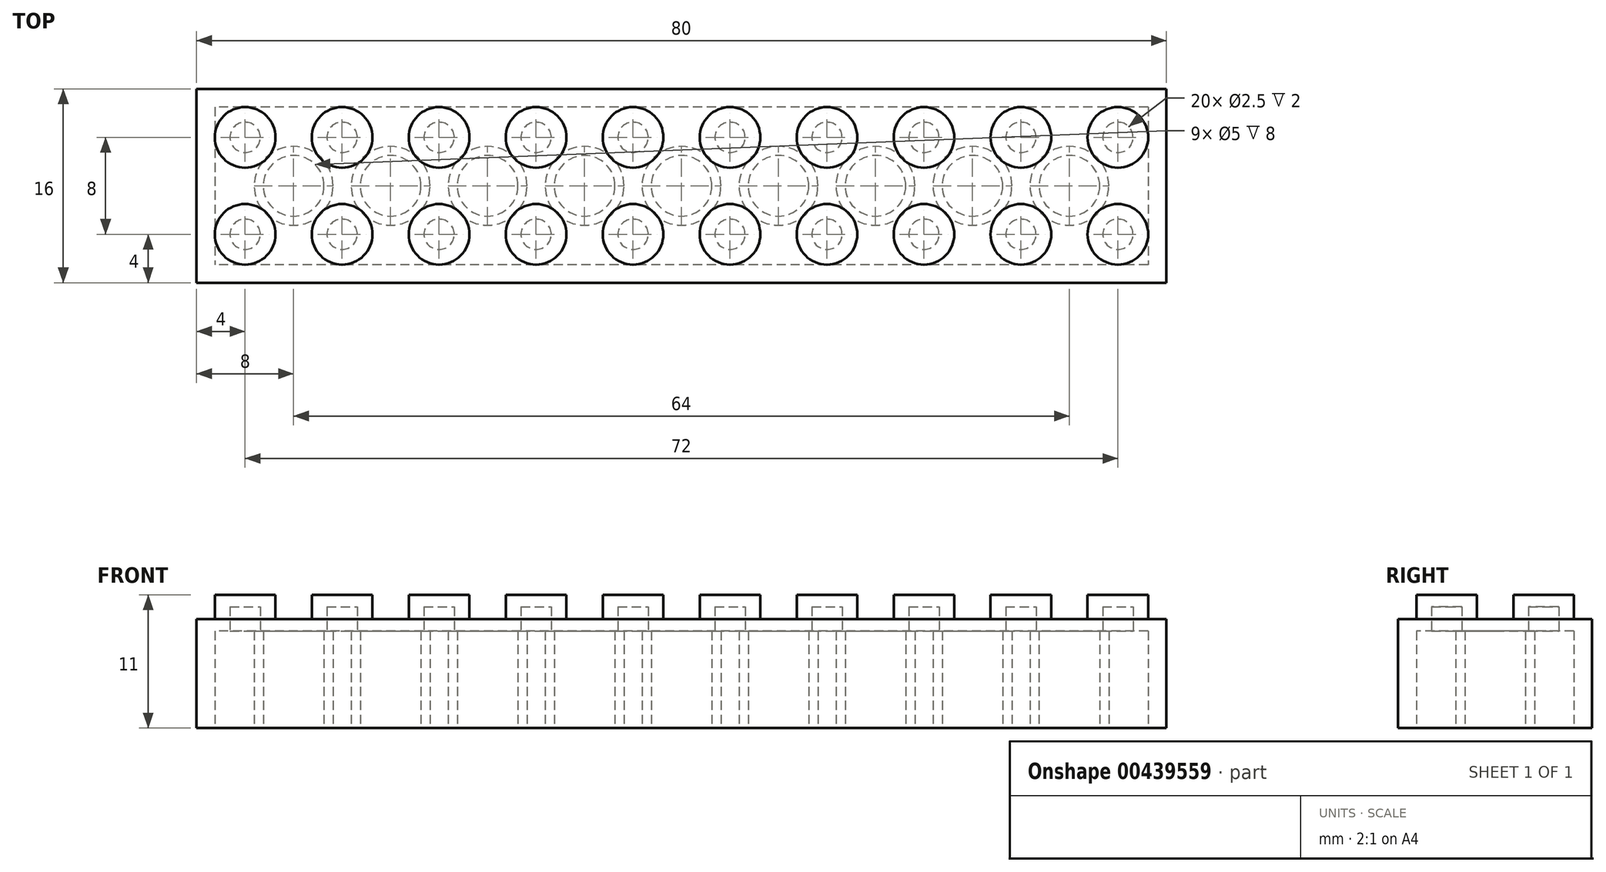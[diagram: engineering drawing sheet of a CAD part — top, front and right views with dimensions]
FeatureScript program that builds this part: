
annotation { "Feature Type Name" : "Feature", "Feature Type Description" : "" }
export const myFeature = defineFeature(function(context is Context, id is Id, definition is map)
    precondition{}
    {
        {
            var Q0;
            Q0=qCreatedBy(makeId("Top.planeOp"),FACE);
            var sketch = newSketch(context, id + "F0", { "sketchPlane" : qUnion([Q0])});
            skLineSegment(sketch, "E0.bottom", {"start": v(40, -8) * mm, "end": v(-40, -8) * mm});
            skLineSegment(sketch, "E0.top", {"start": v(40, 8) * mm, "end": v(-40, 8) * mm});
            skLineSegment(sketch, "E0.left", {"start": v(40, -8) * mm, "end": v(40, 8) * mm});
            skLineSegment(sketch, "E0.right", {"start": v(-40, -8) * mm, "end": v(-40, 8) * mm});
            skPoint(sketch, "E0.middle", {"position": v(0, 0) * mm});
            skSolve(sketch);
        }
        {
            var Q0;
            Q0=makeQuery(id+"F0.imprint","IMPRINT",FACE,{"disambiguationData":[TD([[makeQuery(id+"F0.imprint","IMPRINT",EDGE,{"derivedFrom":sQuery(id+"F0.wireOp",EDGE,"E0.bottom")}),-1.0]])]});
            extrude(context, id + "F1", {"entities" : qUnion([Q0]), "depth" : 9 * mm});
        }
        {
            var Q0;
            Q0=makeQuery(id+"F1.opExtrude","CAP_FACE",FACE,{"disambiguationData":[OSD([sQuery(id+"F0.wireOp",EDGE,"E0.bottom"),sQuery(id+"F0.wireOp",EDGE,"E0.top"),sQuery(id+"F0.wireOp",EDGE,"E0.left"),sQuery(id+"F0.wireOp",EDGE,"E0.right")])],"isStart":false});
            var sketch = newSketch(context, id + "F2", { "sketchPlane" : qUnion([Q0])});
            skCircle(sketch, "E1", {"center": v(-36, 4) * mm, "radius": 2.5 * mm});
            skCircle(sketch, "E2.0.1.0", {"center": v(-36, -4) * mm, "radius": 2.5 * mm});
            skCircle(sketch, "E2.1.0.0", {"center": v(-28, 4) * mm, "radius": 2.5 * mm});
            skCircle(sketch, "E2.1.1.0", {"center": v(-28, -4) * mm, "radius": 2.5 * mm});
            skCircle(sketch, "E2.2.0.0", {"center": v(-20, 4) * mm, "radius": 2.5 * mm});
            skCircle(sketch, "E2.2.1.0", {"center": v(-20, -4) * mm, "radius": 2.5 * mm});
            skCircle(sketch, "E2.3.0.0", {"center": v(-12, 4) * mm, "radius": 2.5 * mm});
            skCircle(sketch, "E2.3.1.0", {"center": v(-12, -4) * mm, "radius": 2.5 * mm});
            skCircle(sketch, "E2.4.0.0", {"center": v(-4, 4) * mm, "radius": 2.5 * mm});
            skCircle(sketch, "E2.4.1.0", {"center": v(-4, -4) * mm, "radius": 2.5 * mm});
            skCircle(sketch, "E2.5.0.0", {"center": v(4, 4) * mm, "radius": 2.5 * mm});
            skCircle(sketch, "E2.5.1.0", {"center": v(4, -4) * mm, "radius": 2.5 * mm});
            skCircle(sketch, "E2.6.0.0", {"center": v(12, 4) * mm, "radius": 2.5 * mm});
            skCircle(sketch, "E2.6.1.0", {"center": v(12, -4) * mm, "radius": 2.5 * mm});
            skCircle(sketch, "E2.7.0.0", {"center": v(20, 4) * mm, "radius": 2.5 * mm});
            skCircle(sketch, "E2.7.1.0", {"center": v(20, -4) * mm, "radius": 2.5 * mm});
            skLineSegment(sketch, "E2.direction1", {"start": v(-36, 4) * mm, "end": v(-28, 4) * mm, "construction": true});
            skLineSegment(sketch, "E2.direction2", {"start": v(-36, 4) * mm, "end": v(-36, -4) * mm, "construction": true});
            skCircle(sketch, "E3.0.8.0", {"center": v(28, 4) * mm, "radius": 2.5 * mm});
            skCircle(sketch, "E3.0.8.1", {"center": v(28, -4) * mm, "radius": 2.5 * mm});
            skCircle(sketch, "E3.0.9.0", {"center": v(36, 4) * mm, "radius": 2.5 * mm});
            skCircle(sketch, "E3.0.9.1", {"center": v(36, -4) * mm, "radius": 2.5 * mm});
            skSolve(sketch);
        }
        {
            var Q0;
            Q0 = qSketchRegion(id + "F2", true);
            extrude(context, id + "F3", {"entities" : qUnion([Q0]), "operationType" : NewBodyOperationType.ADD, "depth" : 2 * mm});
        }
        {
            var Q0;
            Q0=makeQuery(id+"F1.opExtrude","CAP_FACE",FACE,{"disambiguationData":[OSD([sQuery(id+"F0.wireOp",EDGE,"E0.bottom"),sQuery(id+"F0.wireOp",EDGE,"E0.top"),sQuery(id+"F0.wireOp",EDGE,"E0.left"),sQuery(id+"F0.wireOp",EDGE,"E0.right")])],"isStart":true});
            var sketch = newSketch(context, id + "F4", { "sketchPlane" : qUnion([Q0])});
            skLineSegment(sketch, "E4.bottom", {"start": v(38.5, -6.5) * mm, "end": v(-38.5, -6.5) * mm});
            skLineSegment(sketch, "E4.top", {"start": v(38.5, 6.5) * mm, "end": v(-38.5, 6.5) * mm});
            skLineSegment(sketch, "E4.left", {"start": v(38.5, -6.5) * mm, "end": v(38.5, 6.5) * mm});
            skLineSegment(sketch, "E4.right", {"start": v(-38.5, -6.5) * mm, "end": v(-38.5, 6.5) * mm});
            skPoint(sketch, "E4.middle", {"position": v(0, 0) * mm});
            skCircle(sketch, "E5", {"center": v(-32, 0) * mm, "radius": 3.25 * mm});
            skCircle(sketch, "E6", {"center": v(-32, 0) * mm, "radius": 2.5 * mm});
            skCircle(sketch, "E7.1.0.0", {"center": v(-24, 0) * mm, "radius": 3.25 * mm});
            skCircle(sketch, "E7.1.0.1", {"center": v(-24, 0) * mm, "radius": 2.5 * mm});
            skCircle(sketch, "E7.2.0.0", {"center": v(-16, 0) * mm, "radius": 3.25 * mm});
            skCircle(sketch, "E7.2.0.1", {"center": v(-16, 0) * mm, "radius": 2.5 * mm});
            skCircle(sketch, "E7.3.0.0", {"center": v(-8, 0) * mm, "radius": 3.25 * mm});
            skCircle(sketch, "E7.3.0.1", {"center": v(-8, 0) * mm, "radius": 2.5 * mm});
            skCircle(sketch, "E7.4.0.0", {"center": v(0, 0) * mm, "radius": 3.25 * mm});
            skCircle(sketch, "E7.4.0.1", {"center": v(0, 0) * mm, "radius": 2.5 * mm});
            skCircle(sketch, "E7.5.0.0", {"center": v(8, 0) * mm, "radius": 3.25 * mm});
            skCircle(sketch, "E7.5.0.1", {"center": v(8, 0) * mm, "radius": 2.5 * mm});
            skCircle(sketch, "E7.6.0.0", {"center": v(16, 0) * mm, "radius": 3.25 * mm});
            skCircle(sketch, "E7.6.0.1", {"center": v(16, 0) * mm, "radius": 2.5 * mm});
            skLineSegment(sketch, "E7.direction1", {"start": v(-32, 0) * mm, "end": v(-24, 0) * mm, "construction": true});
            skCircle(sketch, "E8.0.7.0", {"center": v(24, 0) * mm, "radius": 3.25 * mm});
            skCircle(sketch, "E8.2.7.0", {"center": v(24, 0) * mm, "radius": 2.5 * mm});
            skCircle(sketch, "E8.0.8.0", {"center": v(32, 0) * mm, "radius": 3.25 * mm});
            skCircle(sketch, "E8.2.8.0", {"center": v(32, 0) * mm, "radius": 2.5 * mm});
            skSolve(sketch);
        }
        {
            var Q0;
            Q0=qSketchRegion(id+"F4",true);
            var Q1;
            Q1=makeQuery(id+"F4.imprint","IMPRINT",FACE,{"disambiguationData":[TD([[makeQuery(id+"F4.imprint","IMPRINT",EDGE,{"derivedFrom":sQuery(id+"F4.wireOp",EDGE,"E6")}),1.0]])]});
            var Q2;
            Q2=makeQuery(id+"F4.imprint","IMPRINT",FACE,{"disambiguationData":[TD([[makeQuery(id+"F4.imprint","IMPRINT",EDGE,{"derivedFrom":sQuery(id+"F4.wireOp",EDGE,"E7.1.0.1")}),1.0]])]});
            var Q3;
            Q3=makeQuery(id+"F4.imprint","IMPRINT",FACE,{"disambiguationData":[TD([[makeQuery(id+"F4.imprint","IMPRINT",EDGE,{"derivedFrom":sQuery(id+"F4.wireOp",EDGE,"E7.2.0.1")}),1.0]])]});
            var Q4;
            Q4=makeQuery(id+"F4.imprint","IMPRINT",FACE,{"disambiguationData":[TD([[makeQuery(id+"F4.imprint","IMPRINT",EDGE,{"derivedFrom":sQuery(id+"F4.wireOp",EDGE,"E7.3.0.1")}),1.0]])]});
            var Q5;
            Q5=makeQuery(id+"F4.imprint","IMPRINT",FACE,{"disambiguationData":[TD([[makeQuery(id+"F4.imprint","IMPRINT",EDGE,{"derivedFrom":sQuery(id+"F4.wireOp",EDGE,"E7.4.0.1")}),1.0]])]});
            var Q6;
            Q6=makeQuery(id+"F4.imprint","IMPRINT",FACE,{"disambiguationData":[TD([[makeQuery(id+"F4.imprint","IMPRINT",EDGE,{"derivedFrom":sQuery(id+"F4.wireOp",EDGE,"E7.5.0.1")}),1.0]])]});
            var Q7;
            Q7=makeQuery(id+"F4.imprint","IMPRINT",FACE,{"disambiguationData":[TD([[makeQuery(id+"F4.imprint","IMPRINT",EDGE,{"derivedFrom":sQuery(id+"F4.wireOp",EDGE,"E7.6.0.1")}),1.0]])]});
            var Q8;
            Q8=makeQuery(id+"F4.imprint","IMPRINT",FACE,{"disambiguationData":[TD([[makeQuery(id+"F4.imprint","IMPRINT",EDGE,{"derivedFrom":sQuery(id+"F4.wireOp",EDGE,"E8.2.7.0")}),1.0]])]});
            var Q9;
            Q9=makeQuery(id+"F4.imprint","IMPRINT",FACE,{"disambiguationData":[TD([[makeQuery(id+"F4.imprint","IMPRINT",EDGE,{"derivedFrom":sQuery(id+"F4.wireOp",EDGE,"E8.2.8.0")}),1.0]])]});
            extrude(context, id + "F5", {"entities" : qUnion([Q0, Q1, Q2, Q3, Q4, Q5, Q6, Q7, Q8, Q9]), "operationType" : NewBodyOperationType.REMOVE, "oppositeDirection" : true, "depth" : 8 * mm});
        }
        {
            var Q0;
            {var subQ0=sQuery(id+"F0.wireOp",EDGE,"E0.left");var subQ1=sQuery(id+"F0.wireOp",EDGE,"E0.top");var subQ2=sQuery(id+"F0.wireOp",EDGE,"E0.right");var subQ3=sQuery(id+"F0.wireOp",EDGE,"E0.bottom");Q0=makeQuery(id+"F5.boolean.opBoolean","SPLIT",FACE,{"disambiguationData":[TD([makeQuery(id+"F1.opExtrude","SWEPT_FACE",FACE,{"disambiguationData":[OSD([subQ3])]})])],"derivedFrom":makeQuery(id+"F1.opExtrude","CAP_FACE",FACE,{"disambiguationData":[OSD([subQ3,subQ1,subQ0,subQ2])],"isStart":true})});}
            var sketch = newSketch(context, id + "F6", { "sketchPlane" : qUnion([Q0])});
            skCircle(sketch, "E9", {"center": v(-36, 4) * mm, "radius": 1.25 * mm});
            skCircle(sketch, "E10.0.1.0", {"center": v(-36, -4) * mm, "radius": 1.25 * mm});
            skCircle(sketch, "E10.1.0.0", {"center": v(-28, 4) * mm, "radius": 1.25 * mm});
            skCircle(sketch, "E10.1.1.0", {"center": v(-28, -4) * mm, "radius": 1.25 * mm});
            skCircle(sketch, "E10.2.0.0", {"center": v(-20, 4) * mm, "radius": 1.25 * mm});
            skCircle(sketch, "E10.2.1.0", {"center": v(-20, -4) * mm, "radius": 1.25 * mm});
            skCircle(sketch, "E10.3.0.0", {"center": v(-12, 4) * mm, "radius": 1.25 * mm});
            skCircle(sketch, "E10.3.1.0", {"center": v(-12, -4) * mm, "radius": 1.25 * mm});
            skCircle(sketch, "E10.4.0.0", {"center": v(-4, 4) * mm, "radius": 1.25 * mm});
            skCircle(sketch, "E10.4.1.0", {"center": v(-4, -4) * mm, "radius": 1.25 * mm});
            skCircle(sketch, "E10.5.0.0", {"center": v(4, 4) * mm, "radius": 1.25 * mm});
            skCircle(sketch, "E10.5.1.0", {"center": v(4, -4) * mm, "radius": 1.25 * mm});
            skCircle(sketch, "E10.6.0.0", {"center": v(12, 4) * mm, "radius": 1.25 * mm});
            skCircle(sketch, "E10.6.1.0", {"center": v(12, -4) * mm, "radius": 1.25 * mm});
            skCircle(sketch, "E10.7.0.0", {"center": v(20, 4) * mm, "radius": 1.25 * mm});
            skCircle(sketch, "E10.7.1.0", {"center": v(20, -4) * mm, "radius": 1.25 * mm});
            skLineSegment(sketch, "E10.direction1", {"start": v(-36, 4) * mm, "end": v(-28, 4) * mm, "construction": true});
            skLineSegment(sketch, "E10.direction2", {"start": v(-36, 4) * mm, "end": v(-36, -4) * mm, "construction": true});
            skCircle(sketch, "E11.0.8.0", {"center": v(28, 4) * mm, "radius": 1.25 * mm});
            skCircle(sketch, "E11.0.8.1", {"center": v(28, -4) * mm, "radius": 1.25 * mm});
            skCircle(sketch, "E11.0.9.0", {"center": v(36, 4) * mm, "radius": 1.25 * mm});
            skCircle(sketch, "E11.0.9.1", {"center": v(36, -4) * mm, "radius": 1.25 * mm});
            skSolve(sketch);
        }
        {
            var Q0;
            Q0=qSketchRegion(id+"F6",true);
            extrude(context, id + "F7", {"entities" : qUnion([Q0]), "operationType" : NewBodyOperationType.REMOVE, "oppositeDirection" : true, "depth" : 10 * mm});
        }
    });
